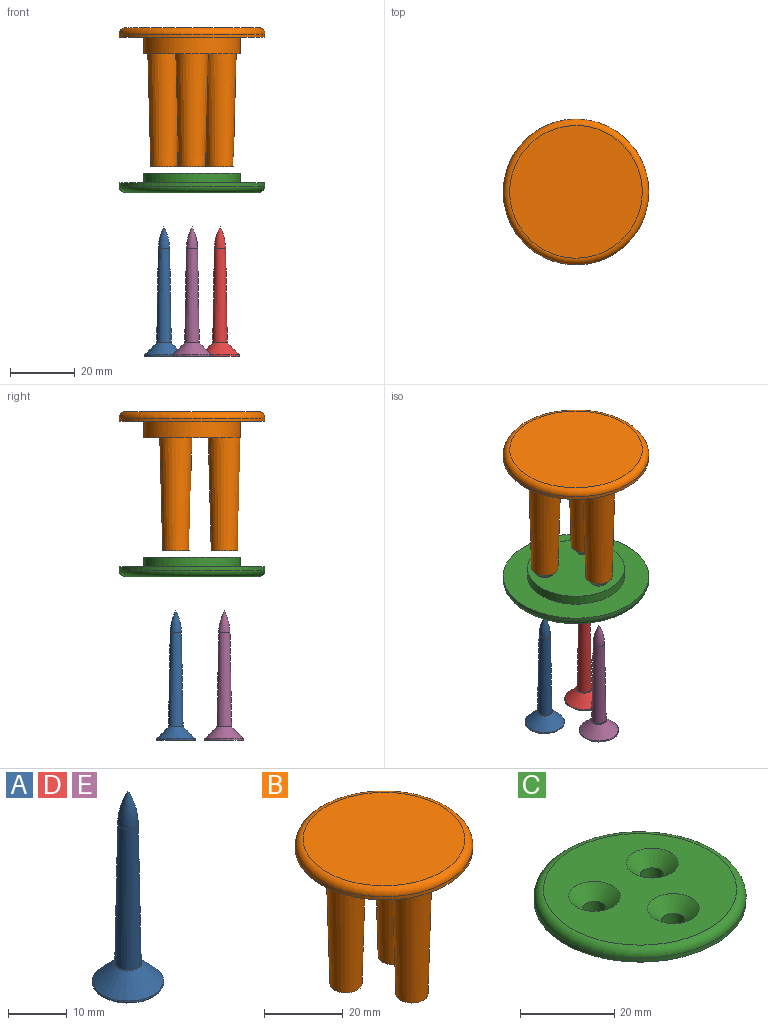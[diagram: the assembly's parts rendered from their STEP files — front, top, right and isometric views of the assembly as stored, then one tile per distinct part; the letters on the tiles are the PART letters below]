
ASSEMBLY  parts=5 mates=4
PART A: 13 faces, bbox 13.2x13.2x40 mm
  f0: plane 11.55x11.55mm, normal (0,0,-1), area 90.9mm2, adj f4,f5,f6,f7,f8,f9,f11
  f1: cone r=6.5mm half-angle=45deg, axis (0,0,-1), area 135.1mm2, adj f11,f12
  f2: cone r=2.25mm half-angle=1deg, axis (0,0,-1), area 362.4mm2, adj f3,f12
  f3: revolved ~6.78x3.5mm, area 50.7mm2, adj f2
  f4: plane 3x2.31mm, normal (0,-1,0), area 6.9mm2, adj f0,f5,f9,f10
  f5: plane 3x2mm, normal (-0.87,-0.5,0), area 6.9mm2, adj f0,f4,f6,f10
  f6: plane 3x2mm, normal (-0.87,0.5,0), area 6.9mm2, adj f0,f5,f7,f10
  f7: plane 3x2.31mm, normal (0,1,0), area 6.9mm2, adj f0,f6,f8,f10
  f8: plane 3x2mm, normal (0.87,0.5,0), area 6.9mm2, adj f0,f7,f9,f10
  f9: plane 3x2mm, normal (0.87,-0.5,0), area 6.9mm2, adj f0,f4,f8,f10
  f10: plane 4.62x4mm, normal (0,0,-1), area 13.9mm2, adj f4,f5,f6,f7,f8,f9
  f11: torus R=5.78mm, axis (0,0,-1), area 26.6mm2, adj f0,f1
  f12: torus R=2.55mm, axis (0,0,-1), area 3.3mm2, adj f1,f2
PART B: 18 faces, bbox 48.7x48.7x43 mm
  f0: cylinder r=15mm len=30mm, axis (0,0,-1), area 471.2mm2, adj f1,f4
  f1: plane 30x30mm, normal (0,0,-1), area 471.2mm2, adj f0,f6,f8,f10
  f2: cylinder r=22.5mm len=45mm, axis (0,0,-1), area 141.4mm2, adj f4,f5
  f3: plane 41x41mm, normal (0,0,1), area 1320.3mm2, adj f5
  f4: plane 45x45mm, normal (0,0,-1), area 883.6mm2, adj f0,f2
  f5: torus R=20.5mm, axis (0,0,1), area 429.8mm2, adj f2,f3
  f6: cone r=5mm half-angle=1.5deg, axis (0,0,1), area 999.1mm2, adj f1,f7
  f7: plane 8.17x8.17mm, normal (0,0,-1), area 42.8mm2, adj f6,f16
  f8: cone r=5mm half-angle=1.5deg, axis (0,0,1), area 999.1mm2, adj f1,f9
  f9: plane 8.17x8.17mm, normal (0,0,-1), area 42.8mm2, adj f8,f14
  f10: cone r=5mm half-angle=1.5deg, axis (0,0,1), area 999.1mm2, adj f1,f11
  f11: plane 8.17x8.17mm, normal (0,0,-1), area 42.8mm2, adj f10,f12
  f12: cylinder r=1.75mm len=30mm, axis (0,0,-1), area 329.9mm2, adj f11,f13
  f13: plane 3.5x3.5mm, normal (0,0,-1), area 9.6mm2, adj f12
  f14: cylinder r=1.75mm len=30mm, axis (0,0,-1), area 329.9mm2, adj f9,f15
  f15: plane 3.5x3.5mm, normal (0,0,-1), area 9.6mm2, adj f14
  f16: cylinder r=1.75mm len=30mm, axis (0,0,-1), area 329.9mm2, adj f7,f17
  f17: plane 3.5x3.5mm, normal (0,0,-1), area 9.6mm2, adj f16
PART C: 12 faces, bbox 48.7x48.7x6 mm
  f0: cylinder r=15mm len=30mm, axis (0,0,-1), area 282.7mm2, adj f1,f4
  f1: plane 30x30mm, normal (0,0,-1), area 648mm2, adj f0,f6,f7,f8
  f2: cylinder r=22.5mm len=45mm, axis (0,0,-1), area 141.4mm2, adj f4,f5
  f3: plane 41x41mm, normal (0,0,1), area 1035.2mm2, adj f5,f9,f10,f11
  f4: plane 45x45mm, normal (0,0,-1), area 883.6mm2, adj f0,f2
  f5: torus R=20.5mm, axis (0,0,1), area 429.8mm2, adj f2,f3
  f6: cylinder r=2.5mm len=5mm, axis (0,0,-1), area 47.1mm2, adj f1,f10
  f7: cylinder r=2.5mm len=5mm, axis (0,0,-1), area 47.1mm2, adj f1,f11
  f8: cylinder r=2.5mm len=5mm, axis (0,0,-1), area 47.1mm2, adj f1,f9
  f9: cone r=2.5mm half-angle=45deg, axis (0,0,1), area 106.6mm2, adj f3,f8
  f10: cone r=2.5mm half-angle=45deg, axis (0,0,1), area 106.6mm2, adj f3,f6
  f11: cone r=2.5mm half-angle=45deg, axis (0,0,1), area 106.6mm2, adj f3,f7
PART D: same geometry as A
PART E: same geometry as A
PLACE A rot(axis=(0,0,-1),154.3deg) t=(-8.66,5,-93.64)mm
PLACE B at identity
PLACE C rot(axis=(0.87,-0.5,0),180deg) t=(0,0,-37)mm
PLACE D rot(axis=(0,0,1),85.7deg) t=(8.66,5,-93.64)mm
PLACE E rot(axis=(0,0,-1),34.3deg) t=(0,-10,-93.64)mm
MATE cylindrical D.f1 <-> C.f8  axis (0,0,-1) through (8.66,5,-89.47)mm
MATE planar C.f2 <-> B.f2  axis (0,0,1) through (0,0,-40)mm
MATE cylindrical C.f8 <-> B.f10  axis (0,0,1) through (8.66,5,-40)mm
MATE cylindrical C.f0 <-> B.f2  axis (0,0,1) through (0,0,-38.5)mm
